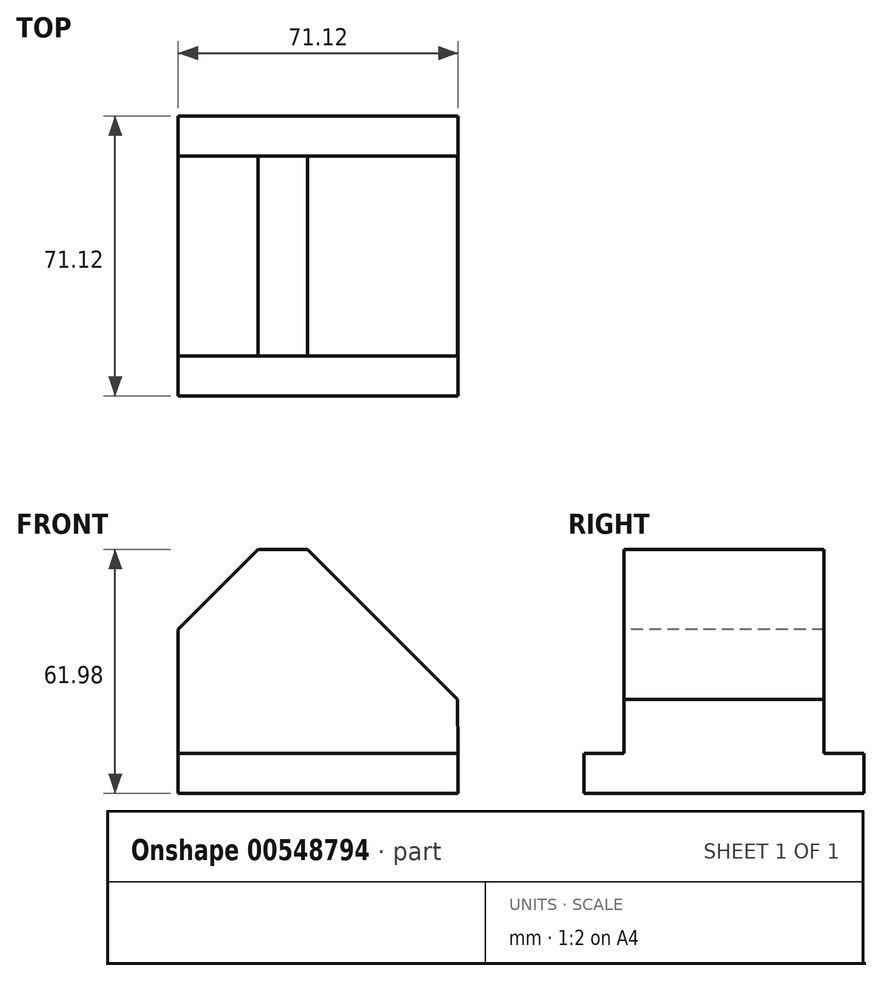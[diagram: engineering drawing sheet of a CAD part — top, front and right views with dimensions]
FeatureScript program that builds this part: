
annotation { "Feature Type Name" : "Feature", "Feature Type Description" : "" }
export const myFeature = defineFeature(function(context is Context, id is Id, definition is map)
    precondition{}
    {
        {
            var Q0;
            Q0=qCreatedBy(makeId("Top.planeOp"),FACE);
            var sketch = newSketch(context, id + "F0", { "sketchPlane" : qUnion([Q0])});
            skLineSegment(sketch, "E0.bottom", {"start": v(-54.28, 62.56) * mm, "end": v(16.84, 62.56) * mm});
            skLineSegment(sketch, "E0.top", {"start": v(-54.28, -8.56) * mm, "end": v(16.84, -8.56) * mm});
            skLineSegment(sketch, "E0.left", {"start": v(-54.28, 62.56) * mm, "end": v(-54.28, -8.56) * mm});
            skLineSegment(sketch, "E0.right", {"start": v(16.84, 62.56) * mm, "end": v(16.84, -8.56) * mm});
            skSolve(sketch);
        }
        {
            var Q0;
            Q0 = qSketchRegion(id + "F0", true);
            extrude(context, id + "F1", {"entities" : qUnion([Q0]), "depth" : 61.98 * mm, "offsetDistance" : 25.4 * mm});
        }
        {
            var Q0;
            Q0=makeQuery(id+"F1.opExtrude","SWEPT_FACE",FACE,{"disambiguationData":[OSD([sQuery(id+"F0.wireOp",EDGE,"E0.top")])]});
            var sketch = newSketch(context, id + "F2", { "sketchPlane" : qUnion([Q0])});
            skLineSegment(sketch, "E1.bottom", {"start": v(-54.28, 0) * mm, "end": v(16.84, 0) * mm});
            skLineSegment(sketch, "E1.top", {"start": v(-54.28, 0) * mm, "end": v(16.84, 0) * mm});
            skLineSegment(sketch, "E1.left", {"start": v(-54.28, 0) * mm, "end": v(-54.28, 0) * mm});
            skLineSegment(sketch, "E1.right", {"start": v(16.84, 0) * mm, "end": v(16.84, 0) * mm});
            skLineSegment(sketch, "E2.top", {"start": v(-54.28, 10.16) * mm, "end": v(16.84, 10.16) * mm});
            skLineSegment(sketch, "E2.left", {"start": v(-54.28, 0) * mm, "end": v(-54.28, 10.16) * mm});
            skLineSegment(sketch, "E2.right", {"start": v(16.84, 0) * mm, "end": v(16.84, 10.16) * mm});
            skSolve(sketch);
        }
        {
            var Q0;
            {var subQ0=sQuery(id+"F2.wireOp",EDGE,"E2.top");Q0=makeQuery(id+"F2.imprint","IMPRINT",FACE,{"disambiguationData":[TD([[makeQuery(id+"F2.imprint","IMPRINT",EDGE,{"derivedFrom":subQ0}),1.0]])]});}
            extrude(context, id + "F3", {"entities" : qUnion([Q0]), "operationType" : NewBodyOperationType.REMOVE, "oppositeDirection" : true, "depth" : 10.16 * mm, "offsetDistance" : 25.4 * mm});
        }
        {
            var Q0;
            Q0=makeQuery(id+"F1.opExtrude","SWEPT_FACE",FACE,{"disambiguationData":[OSD([sQuery(id+"F0.wireOp",EDGE,"E0.bottom")])]});
            var sketch = newSketch(context, id + "F4", { "sketchPlane" : qUnion([Q0])});
            skLineSegment(sketch, "E3.bottom", {"start": v(-16.84, 0) * mm, "end": v(54.28, 0) * mm});
            skLineSegment(sketch, "E3.top", {"start": v(-16.84, 0) * mm, "end": v(54.28, 0) * mm});
            skLineSegment(sketch, "E3.left", {"start": v(-16.84, 0) * mm, "end": v(-16.84, 0) * mm});
            skLineSegment(sketch, "E3.right", {"start": v(54.28, 0) * mm, "end": v(54.28, 0) * mm});
            skLineSegment(sketch, "E4.bottom", {"start": v(54.28, 0) * mm, "end": v(-16.84, 0) * mm});
            skLineSegment(sketch, "E4.top", {"start": v(54.28, 10.16) * mm, "end": v(-16.84, 10.16) * mm});
            skLineSegment(sketch, "E4.left", {"start": v(54.28, 0) * mm, "end": v(54.28, 10.16) * mm});
            skLineSegment(sketch, "E4.right", {"start": v(-16.84, 0) * mm, "end": v(-16.84, 10.16) * mm});
            skSolve(sketch);
        }
        {
            var Q0;
            {var subQ0=sQuery(id+"F4.wireOp",EDGE,"E4.top");Q0=makeQuery(id+"F4.imprint","IMPRINT",FACE,{"disambiguationData":[TD([[makeQuery(id+"F4.imprint","IMPRINT",EDGE,{"derivedFrom":subQ0}),-1.0]])]});}
            extrude(context, id + "F5", {"entities" : qUnion([Q0]), "operationType" : NewBodyOperationType.REMOVE, "oppositeDirection" : true, "depth" : 10.16 * mm, "offsetDistance" : 25.4 * mm});
        }
        {
            var Q0;
            Q0=makeQuery(id+"F3.boolean.opBoolean","COPY",FACE,{"derivedFrom":makeQuery(id+"F3.opExtrude","CAP_FACE",FACE,{"disambiguationData":[OSD([sQuery(id+"F0.wireOp",EDGE,"E0.top"),sQuery(id+"F0.wireOp",EDGE,"E0.left"),sQuery(id+"F0.wireOp",EDGE,"E0.right"),sQuery(id+"F2.wireOp",EDGE,"E2.top")])],"isStart":false})});
            var sketch = newSketch(context, id + "F6", { "sketchPlane" : qUnion([Q0])});
            skLineSegment(sketch, "E5", {"start": v(-54.28, 61.98) * mm, "end": v(-33.96, 61.98) * mm});
            skLineSegment(sketch, "E6", {"start": v(-33.96, 61.98) * mm, "end": v(-54.28, 41.66) * mm});
            skSolve(sketch);
        }
        {
            var Q0;
            Q0 = qSketchRegion(id + "F6", true);
            var Q1;
            {var subQ0=sQuery(id+"F6.wireOp",EDGE,"E5");Q1=makeQuery(id+"F6.imprint","IMPRINT",FACE,{"disambiguationData":[TD([[makeQuery(id+"F6.imprint","IMPRINT",EDGE,{"derivedFrom":subQ0}),-1.0]])]});}
            extrude(context, id + "F7", {"entities" : qUnion([Q0, Q1]), "operationType" : NewBodyOperationType.REMOVE, "oppositeDirection" : true, "depth" : 76.2 * mm, "offsetDistance" : 25.4 * mm});
        }
        {
            var Q0;
            Q0=makeQuery(id+"F3.boolean.opBoolean","COPY",FACE,{"derivedFrom":makeQuery(id+"F3.opExtrude","CAP_FACE",FACE,{"disambiguationData":[OSD([sQuery(id+"F0.wireOp",EDGE,"E0.top"),sQuery(id+"F0.wireOp",EDGE,"E0.left"),sQuery(id+"F0.wireOp",EDGE,"E0.right"),sQuery(id+"F2.wireOp",EDGE,"E2.top")])],"isStart":false})});
            var sketch = newSketch(context, id + "F8", { "sketchPlane" : qUnion([Q0])});
            skLineSegment(sketch, "E7", {"start": v(16.73, 23.88) * mm, "end": v(16.84, 10.16) * mm});
            skLineSegment(sketch, "E8", {"start": v(16.73, 23.88) * mm, "end": v(-21.37, 61.98) * mm});
            skSolve(sketch);
        }
        {
            var Q0;
            Q0=makeQuery(id+"F8.imprint","IMPRINT",FACE,{"disambiguationData":[TD([[makeQuery(id+"F8.imprint","IMPRINT",EDGE,{"derivedFrom":sQuery(id+"F8.wireOp",EDGE,"E7")}),1.0]])]});
            extrude(context, id + "F9", {"entities" : qUnion([Q0]), "operationType" : NewBodyOperationType.REMOVE, "oppositeDirection" : true, "depth" : 76.2 * mm, "offsetDistance" : 25.4 * mm});
        }
        {
            var Q0;
            Q0=makeQuery(id+"F9.boolean.opBoolean","COPY",FACE,{"derivedFrom":makeQuery(id+"F9.opExtrude","SWEPT_FACE",FACE,{"disambiguationData":[OSD([sQuery(id+"F8.wireOp",EDGE,"E8")])]})});
            var sketch = newSketch(context, id + "F10", { "sketchPlane" : qUnion([Q0])});
            skCircle(sketch, "E9", {"center": v(-33.98, 26.51) * mm, "radius": 19.05 * mm});
            skSolve(sketch);
        }
        {
            var Q0;
            Q0=makeQuery(id+"F10.imprint","IMPRINT",FACE,{"disambiguationData":[TD([[makeQuery(id+"F10.imprint","IMPRINT",EDGE,{"derivedFrom":sQuery(id+"F10.wireOp",EDGE,"E9")}),1.0]])]});
            extrude(context, id + "F11", {"entities" : qUnion([Q0]), "operationType" : NewBodyOperationType.REMOVE, "oppositeDirection" : true, "depth" : 76.2 * mm, "offsetDistance" : 25.4 * mm});
        }
    });
